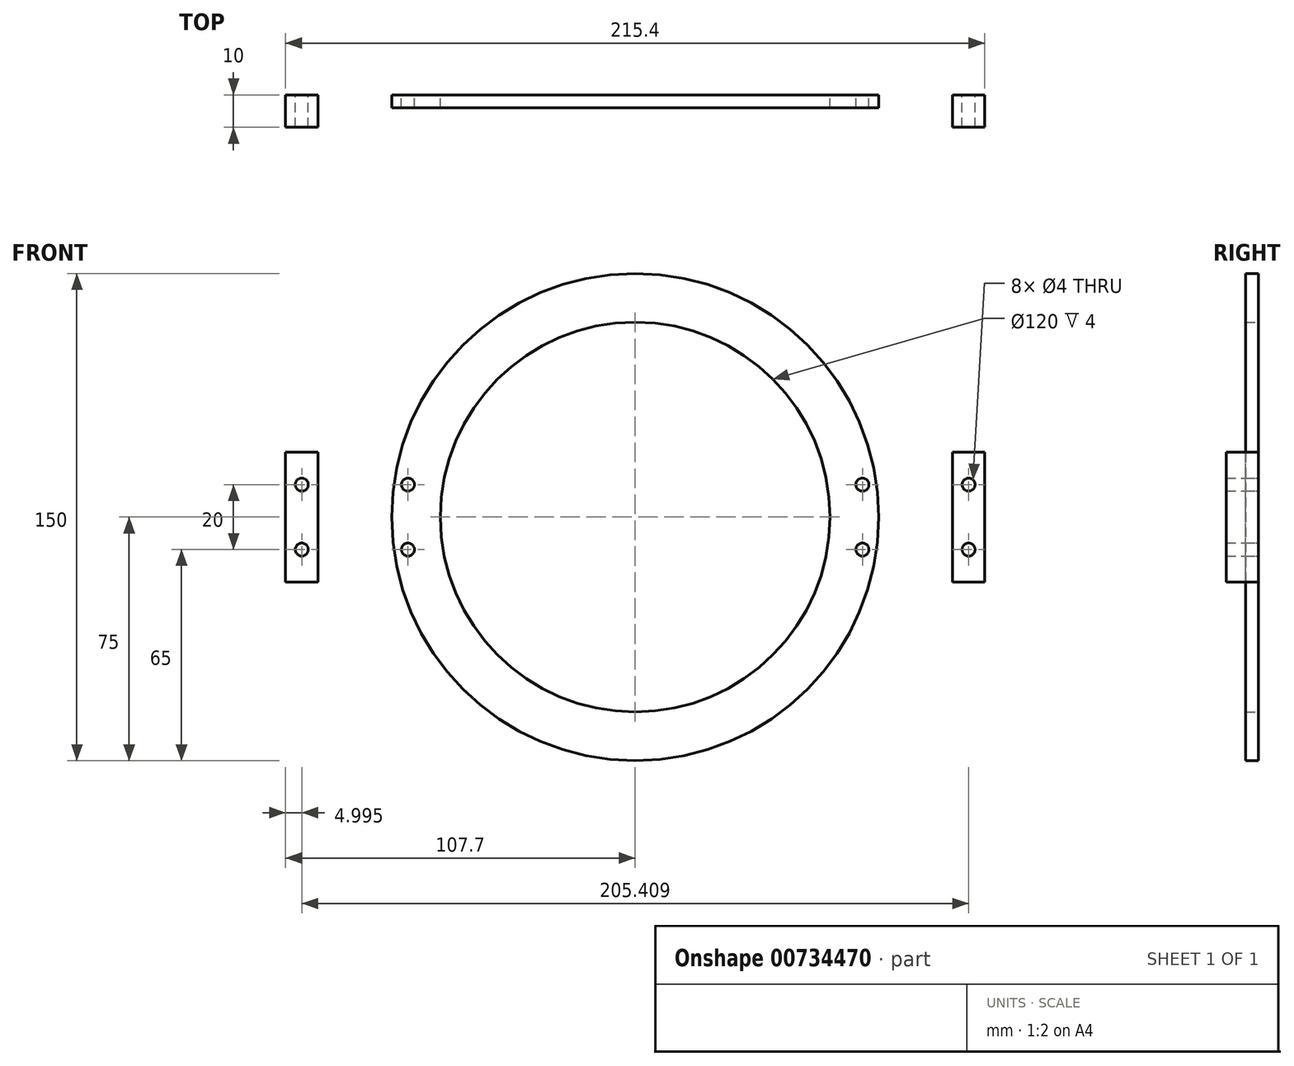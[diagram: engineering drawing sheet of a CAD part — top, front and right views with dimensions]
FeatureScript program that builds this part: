
annotation { "Feature Type Name" : "Feature", "Feature Type Description" : "" }
export const myFeature = defineFeature(function(context is Context, id is Id, definition is map)
    precondition{}
    {
        {
            var Q0;
            Q0=qCreatedBy(makeId("Front.planeOp"),FACE);
            var sketch = newSketch(context, id + "F0", { "sketchPlane" : qUnion([Q0])});
            skCircle(sketch, "E0", {"center": v(0, 0) * mm, "radius": 60 * mm});
            skCircle(sketch, "E1", {"center": v(0, 0) * mm, "radius": 75 * mm});
            skLineSegment(sketch, "E2", {"start": v(-90.44, 0) * mm, "end": v(121.7, 0) * mm, "construction": true});
            skCircle(sketch, "E3", {"center": v(70, 10) * mm, "radius": 2 * mm});
            skCircle(sketch, "E4.MirrorC", {"center": v(70, -10) * mm, "radius": 2 * mm});
            skCircle(sketch, "E5.MirrorC", {"center": v(-70, 10) * mm, "radius": 2 * mm});
            skCircle(sketch, "E6.MirrorC", {"center": v(-70, -10) * mm, "radius": 2 * mm});
            skSolve(sketch);
        }
        {
            var Q0;
            Q0 = qSketchRegion(id + "F0", true);
            extrude(context, id + "F1", {"entities" : qUnion([Q0]), "depth" : 4 * mm, "offsetDistance" : 25 * mm});
        }
        {
            var Q0;
            Q0=qCreatedBy(makeId("Front.planeOp"),FACE);
            var sketch = newSketch(context, id + "F2", { "sketchPlane" : qUnion([Q0])});
            skLineSegment(sketch, "E7.bottom", {"start": v(-107.7, 20) * mm, "end": v(-97.7, 20) * mm});
            skLineSegment(sketch, "E7.top", {"start": v(-107.7, -20) * mm, "end": v(-97.7, -20) * mm});
            skLineSegment(sketch, "E7.left", {"start": v(-107.7, 20) * mm, "end": v(-107.7, -20) * mm});
            skLineSegment(sketch, "E7.right", {"start": v(-97.7, 20) * mm, "end": v(-97.7, -20) * mm});
            skLineSegment(sketch, "E8.MirrorCS", {"start": v(97.7, 20) * mm, "end": v(97.7, -20) * mm});
            skLineSegment(sketch, "E9.MirrorCS", {"start": v(107.7, 20) * mm, "end": v(97.7, 20) * mm});
            skLineSegment(sketch, "E10.MirrorCS", {"start": v(107.7, 20) * mm, "end": v(107.7, -20) * mm});
            skLineSegment(sketch, "E11.MirrorCS", {"start": v(107.7, -20) * mm, "end": v(97.7, -20) * mm});
            skCircle(sketch, "E12", {"center": v(-102.7, 10) * mm, "radius": 2 * mm});
            skLineSegment(sketch, "E13", {"start": v(-91.76, 0) * mm, "end": v(-112.44, 0) * mm, "construction": true});
            skPoint(sketch, "E13.startSnap0", {"position": v(-97.7, 0) * mm});
            skCircle(sketch, "E14.MirrorC", {"center": v(-102.7, -10) * mm, "radius": 2 * mm});
            skCircle(sketch, "E15.MirrorC", {"center": v(102.7, 10) * mm, "radius": 2 * mm});
            skCircle(sketch, "E16.MirrorC", {"center": v(102.7, -10) * mm, "radius": 2 * mm});
            skSolve(sketch);
        }
        {
            var Q0;
            Q0 = qSketchRegion(id + "F2", true);
            extrude(context, id + "F3", {"entities" : qUnion([Q0]), "depth" : 10 * mm, "offsetDistance" : 25 * mm});
        }
    });
